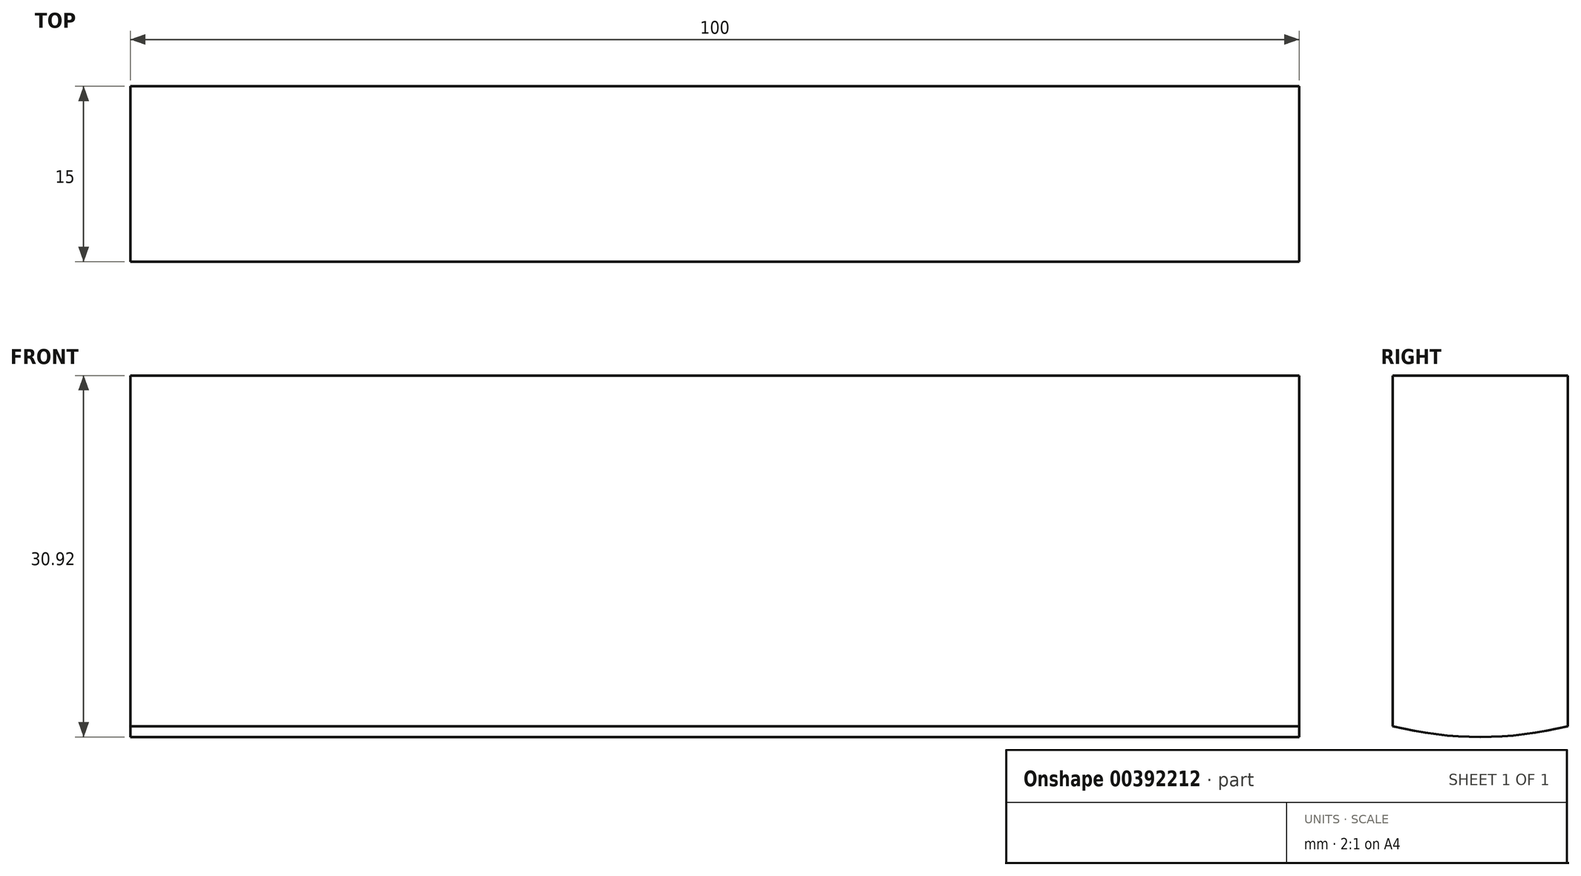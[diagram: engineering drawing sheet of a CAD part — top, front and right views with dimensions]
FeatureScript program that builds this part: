
annotation { "Feature Type Name" : "Feature", "Feature Type Description" : "" }
export const myFeature = defineFeature(function(context is Context, id is Id, definition is map)
    precondition{}
    {
        {
            var Q0;
            Q0=qCreatedBy(makeId("Right.planeOp"),FACE);
            var sketch = newSketch(context, id + "F0", { "sketchPlane" : qUnion([Q0])});
            skLineSegment(sketch, "E0.bottom", {"start": v(-7.5, -15) * mm, "end": v(7.5, -15) * mm, "construction": true});
            skLineSegment(sketch, "E0.top", {"start": v(-7.5, 15) * mm, "end": v(7.5, 15) * mm});
            skLineSegment(sketch, "E0.left", {"start": v(-7.5, -15) * mm, "end": v(-7.5, 15) * mm});
            skLineSegment(sketch, "E0.right", {"start": v(7.5, -15) * mm, "end": v(7.5, 15) * mm});
            skPoint(sketch, "E0.middle", {"position": v(0, 0) * mm});
            skArc(sketch, "E1", {"start": v(-7.5, -15) * mm, "mid": v(0, -15.92) * mm, "end": v(7.5, -15) * mm});
            skSolve(sketch);
        }
        {
            var Q0;
            Q0 = qSketchRegion(id + "F0", true);
            extrude(context, id + "F1", {"entities" : qUnion([Q0]), "depth" : 100 * mm});
        }
    });
